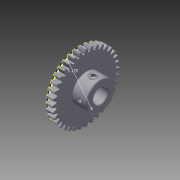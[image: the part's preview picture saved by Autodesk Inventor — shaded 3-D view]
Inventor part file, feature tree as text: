
AUTODESK INVENTOR PART (.ipt)
format: ipt  version: 2012 (Build 160160000, 160)  size: 1,205,248 bytes
history: native  units: in
note: dims shown in document units (in); Inventor stores cm internally (conversion verified against a paired STEP export)
features: other x4, sketch x1
ambient origin geometry x8: Origin, YZ Plane, XZ Plane, XY Plane, X Axis, Y Axis, Z Axis, Center Point
bodies: Solid1 (feature_tree), Solid2 (feature_tree)
feature tree (5):
  other  "s1066z-032s036.ipt"
  other  "71578::s1066z-032s036.ipt"
  other  "71578_1::s1066z-032s036.ipt"
  sketch  "Sketch1"  dims[d0=0.3937in]
  other  "TaggingFeature1"
